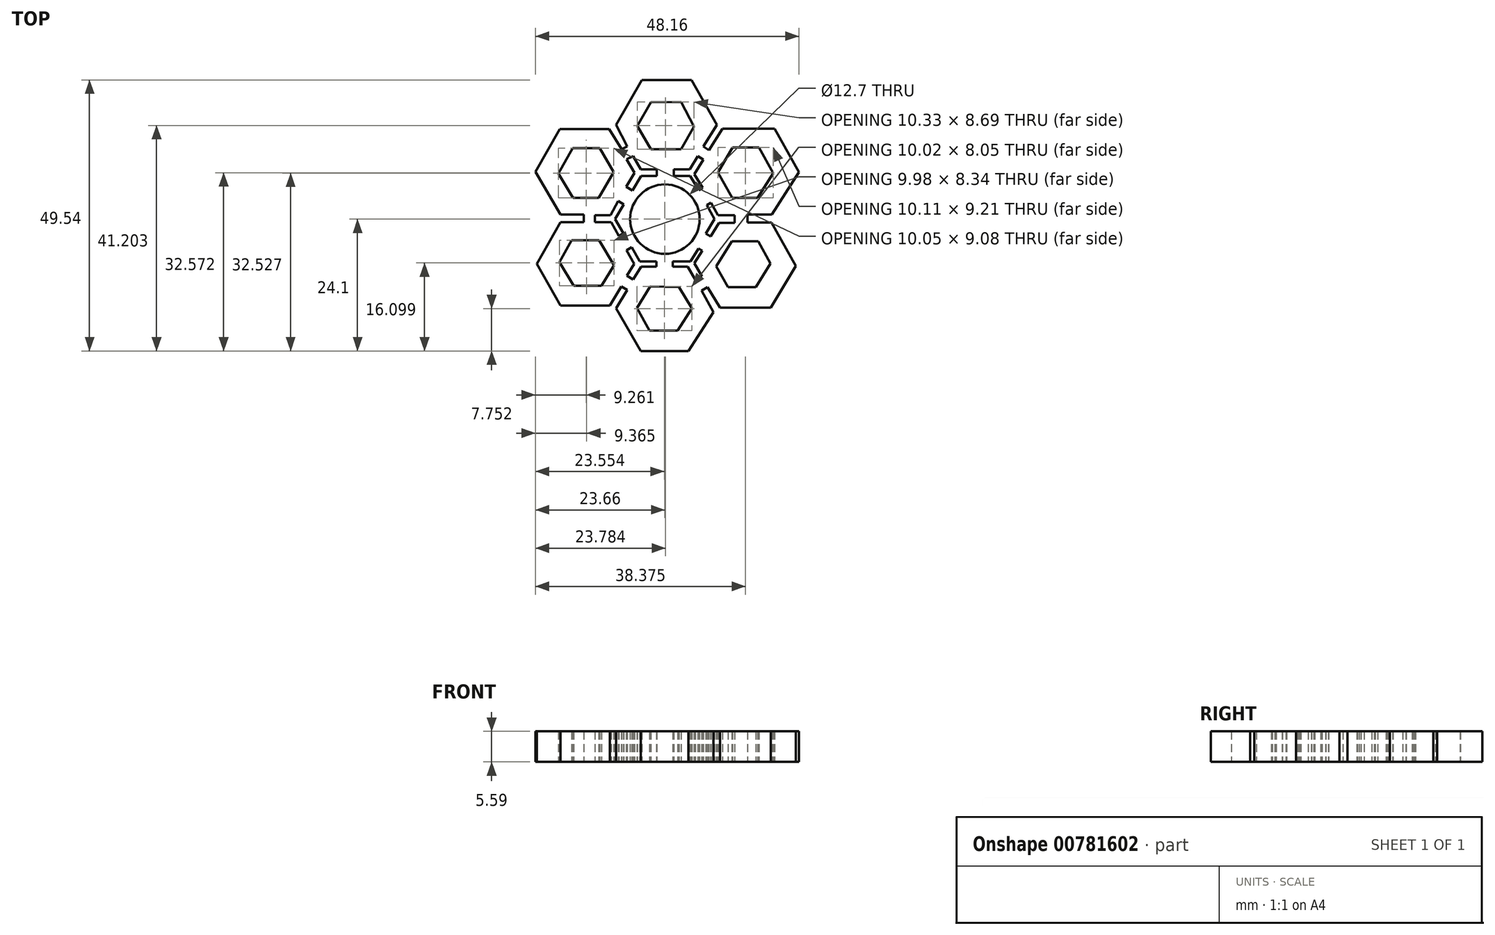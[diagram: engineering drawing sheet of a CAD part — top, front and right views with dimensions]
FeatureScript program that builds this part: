
annotation { "Feature Type Name" : "Feature", "Feature Type Description" : "" }
export const myFeature = defineFeature(function(context is Context, id is Id, definition is map)
    precondition{}
    {
        {
            var Q0;
            Q0=qCreatedBy(makeId("Top.planeOp"),FACE);
            var sketch = newSketch(context, id + "F0", { "sketchPlane" : qUnion([Q0])});
            skCircle(sketch, "E0", {"center": v(0, 0) * mm, "radius": 2.21 * mm});
            skCircle(sketch, "E1", {"center": v(0, 0) * mm, "radius": 6.35 * mm});
            skLineSegment(sketch, "E2", {"start": v(-4.23, 25.44) * mm, "end": v(4.85, 25.44) * mm});
            skLineSegment(sketch, "E3", {"start": v(4.85, 25.44) * mm, "end": v(9.52, 17.24) * mm});
            skLineSegment(sketch, "E4", {"start": v(9.52, 17.24) * mm, "end": v(7.02, 13.29) * mm});
            skLineSegment(sketch, "E5", {"start": v(-4.23, 25.44) * mm, "end": v(-8.93, 17.24) * mm});
            skLineSegment(sketch, "E6", {"start": v(-8.93, 17.24) * mm, "end": v(-6.9, 13.29) * mm});
            skLineSegment(sketch, "E7", {"start": v(7.02, 13.29) * mm, "end": v(8.06, 12.62) * mm});
            skLineSegment(sketch, "E8", {"start": v(8.06, 12.62) * mm, "end": v(10.54, 16.54) * mm});
            skLineSegment(sketch, "E9", {"start": v(-6.9, 13.29) * mm, "end": v(-7.91, 12.76) * mm});
            skPoint(sketch, "E9.endSnap0", {"position": v(-7.91, 15.26) * mm});
            skLineSegment(sketch, "E10", {"start": v(-10.21, 16.49) * mm, "end": v(-7.91, 12.76) * mm});
            skLineSegment(sketch, "E11", {"start": v(-2.54, 21.38) * mm, "end": v(-5.04, 17) * mm});
            skLineSegment(sketch, "E12", {"start": v(-5.04, 17) * mm, "end": v(-2.59, 12.76) * mm});
            skLineSegment(sketch, "E13", {"start": v(-2.59, 12.76) * mm, "end": v(2.96, 12.76) * mm});
            skLineSegment(sketch, "E14", {"start": v(2.96, 12.76) * mm, "end": v(5.3, 16.88) * mm});
            skLineSegment(sketch, "E15", {"start": v(5.3, 16.88) * mm, "end": v(2.93, 21.45) * mm});
            skLineSegment(sketch, "E16", {"start": v(2.93, 21.45) * mm, "end": v(-2.54, 21.38) * mm});
            skLineSegment(sketch, "E17", {"start": v(-6.98, 10.93) * mm, "end": v(-5.8, 11.55) * mm});
            skLineSegment(sketch, "E18", {"start": v(-5.8, 11.55) * mm, "end": v(-4.43, 9.08) * mm});
            skLineSegment(sketch, "E19", {"start": v(-4.43, 9.08) * mm, "end": v(-1.48, 9.11) * mm});
            skLineSegment(sketch, "E20", {"start": v(-1.48, 9.11) * mm, "end": v(-1.46, 7.92) * mm});
            skLineSegment(sketch, "E21", {"start": v(-1.46, 7.92) * mm, "end": v(-4.37, 7.89) * mm});
            skLineSegment(sketch, "E22", {"start": v(-4.37, 7.89) * mm, "end": v(-5.95, 5.25) * mm});
            skLineSegment(sketch, "E23", {"start": v(-5.95, 5.25) * mm, "end": v(-7.05, 5.9) * mm});
            skLineSegment(sketch, "E24", {"start": v(-7.05, 5.9) * mm, "end": v(-5.53, 8.44) * mm});
            skLineSegment(sketch, "E25", {"start": v(-5.53, 8.44) * mm, "end": v(-6.98, 10.93) * mm});
            skLineSegment(sketch, "E26", {"start": v(-10.21, 16.49) * mm, "end": v(-19.24, 16.49) * mm});
            skLineSegment(sketch, "E27", {"start": v(-16.87, 12.97) * mm, "end": v(-11.93, 12.97) * mm});
            skLineSegment(sketch, "E28", {"start": v(-11.93, 12.97) * mm, "end": v(-9.37, 8.57) * mm});
            skLineSegment(sketch, "E29", {"start": v(-9.37, 8.57) * mm, "end": v(-12.06, 3.89) * mm});
            skLineSegment(sketch, "E30", {"start": v(-12.06, 3.89) * mm, "end": v(-16.8, 3.89) * mm});
            skLineSegment(sketch, "E31", {"start": v(-16.8, 3.89) * mm, "end": v(-19.43, 8.34) * mm});
            skLineSegment(sketch, "E32", {"start": v(-19.43, 8.34) * mm, "end": v(-16.87, 12.97) * mm});
            skLineSegment(sketch, "E33", {"start": v(-19.24, 16.49) * mm, "end": v(-23.66, 8.63) * mm});
            skLineSegment(sketch, "E34", {"start": v(-23.66, 8.63) * mm, "end": v(-19.07, 0.84) * mm});
            skLineSegment(sketch, "E35", {"start": v(-19.07, 0.84) * mm, "end": v(-14.8, 0.84) * mm});
            skLineSegment(sketch, "E36", {"start": v(-14.8, 0.84) * mm, "end": v(-14.8, -0.57) * mm});
            skLineSegment(sketch, "E37", {"start": v(-14.8, -0.57) * mm, "end": v(-19.07, -0.57) * mm});
            skLineSegment(sketch, "E38", {"start": v(1.61, 9.11) * mm, "end": v(1.61, 7.92) * mm});
            skLineSegment(sketch, "E39", {"start": v(1.61, 7.92) * mm, "end": v(4.6, 7.92) * mm});
            skLineSegment(sketch, "E40", {"start": v(4.6, 7.92) * mm, "end": v(6.22, 5.3) * mm});
            skLineSegment(sketch, "E41", {"start": v(6.22, 5.3) * mm, "end": v(6.92, 5.72) * mm});
            skLineSegment(sketch, "E42", {"start": v(6.92, 5.72) * mm, "end": v(5.38, 8.22) * mm});
            skLineSegment(sketch, "E43", {"start": v(5.38, 8.22) * mm, "end": v(7, 10.9) * mm});
            skLineSegment(sketch, "E44", {"start": v(7, 10.9) * mm, "end": v(5.98, 11.52) * mm});
            skLineSegment(sketch, "E45", {"start": v(5.98, 11.52) * mm, "end": v(4.53, 9.11) * mm});
            skLineSegment(sketch, "E46", {"start": v(4.53, 9.11) * mm, "end": v(1.61, 9.11) * mm});
            skLineSegment(sketch, "E47", {"start": v(10.54, 16.54) * mm, "end": v(20.05, 16.54) * mm});
            skLineSegment(sketch, "E48", {"start": v(20.05, 16.54) * mm, "end": v(24.5, 8.6) * mm});
            skLineSegment(sketch, "E49", {"start": v(12.37, 13.07) * mm, "end": v(17.15, 13.07) * mm});
            skLineSegment(sketch, "E50", {"start": v(17.15, 13.07) * mm, "end": v(19.77, 8.4) * mm});
            skLineSegment(sketch, "E51", {"start": v(19.77, 8.4) * mm, "end": v(16.9, 3.87) * mm});
            skLineSegment(sketch, "E52", {"start": v(16.9, 3.87) * mm, "end": v(12.27, 3.87) * mm});
            skLineSegment(sketch, "E53", {"start": v(12.27, 3.87) * mm, "end": v(9.66, 8.52) * mm});
            skLineSegment(sketch, "E54", {"start": v(9.66, 8.52) * mm, "end": v(12.37, 13.07) * mm});
            skLineSegment(sketch, "E55", {"start": v(-8.56, 3.3) * mm, "end": v(-7.5, 2.66) * mm});
            skLineSegment(sketch, "E56", {"start": v(-7.5, 2.66) * mm, "end": v(-9.08, 0) * mm});
            skLineSegment(sketch, "E57", {"start": v(-9.08, 0) * mm, "end": v(-7.61, -2.59) * mm});
            skLineSegment(sketch, "E58", {"start": v(-7.61, -2.59) * mm, "end": v(-8.38, -3.12) * mm});
            skLineSegment(sketch, "E59", {"start": v(-8.38, -3.12) * mm, "end": v(-9.8, -0.58) * mm});
            skLineSegment(sketch, "E60", {"start": v(-9.8, -0.58) * mm, "end": v(-12.79, -0.58) * mm});
            skLineSegment(sketch, "E61", {"start": v(-12.79, -0.58) * mm, "end": v(-12.79, 0.74) * mm});
            skLineSegment(sketch, "E62", {"start": v(-12.79, 0.74) * mm, "end": v(-9.93, 0.74) * mm});
            skLineSegment(sketch, "E63", {"start": v(-9.93, 0.74) * mm, "end": v(-8.56, 3.3) * mm});
            skLineSegment(sketch, "E64", {"start": v(7.68, 2.55) * mm, "end": v(8.43, 2.98) * mm});
            skPoint(sketch, "E64.endSnap0", {"position": v(-8.03, 2.98) * mm});
            skLineSegment(sketch, "E65", {"start": v(8.43, 2.98) * mm, "end": v(9.7, 0.73) * mm});
            skLineSegment(sketch, "E66", {"start": v(9.7, 0.73) * mm, "end": v(12.74, 0.73) * mm});
            skLineSegment(sketch, "E67", {"start": v(12.74, 0.73) * mm, "end": v(12.74, -0.67) * mm});
            skLineSegment(sketch, "E68", {"start": v(12.74, -0.67) * mm, "end": v(9.85, -0.67) * mm});
            skLineSegment(sketch, "E69", {"start": v(9.85, -0.67) * mm, "end": v(8.36, -3.17) * mm});
            skLineSegment(sketch, "E70", {"start": v(8.36, -3.17) * mm, "end": v(7.48, -2.64) * mm});
            skLineSegment(sketch, "E71", {"start": v(7.48, -2.64) * mm, "end": v(9.05, 0) * mm});
            skLineSegment(sketch, "E72", {"start": v(9.05, 0) * mm, "end": v(7.68, 2.55) * mm});
            skLineSegment(sketch, "E73", {"start": v(24.5, 8.6) * mm, "end": v(19.56, 0.82) * mm});
            skLineSegment(sketch, "E74", {"start": v(19.56, 0.82) * mm, "end": v(15.06, 0.82) * mm});
            skLineSegment(sketch, "E75", {"start": v(15.06, 0.82) * mm, "end": v(15.06, -0.61) * mm});
            skLineSegment(sketch, "E76", {"start": v(15.06, -0.61) * mm, "end": v(19.45, -0.61) * mm});
            skLineSegment(sketch, "E77", {"start": v(19.45, -0.61) * mm, "end": v(23.9, -8.54) * mm});
            skLineSegment(sketch, "E78", {"start": v(-19.07, -0.57) * mm, "end": v(-23.37, -8.17) * mm});
            skLineSegment(sketch, "E79", {"start": v(-17.05, -3.83) * mm, "end": v(-12.06, -3.83) * mm});
            skLineSegment(sketch, "E80", {"start": v(-12.06, -3.83) * mm, "end": v(-9.3, -8.43) * mm});
            skLineSegment(sketch, "E81", {"start": v(-9.3, -8.43) * mm, "end": v(-11.58, -12.17) * mm});
            skLineSegment(sketch, "E82", {"start": v(-11.58, -12.17) * mm, "end": v(-16.66, -12.17) * mm});
            skLineSegment(sketch, "E83", {"start": v(-16.66, -12.17) * mm, "end": v(-19.28, -7.83) * mm});
            skLineSegment(sketch, "E84", {"start": v(-19.28, -7.83) * mm, "end": v(-17.05, -3.83) * mm});
            skLineSegment(sketch, "E85", {"start": v(-8, -12.28) * mm, "end": v(-10.06, -15.8) * mm});
            skLineSegment(sketch, "E86", {"start": v(-10.06, -15.8) * mm, "end": v(-19.05, -15.8) * mm});
            skLineSegment(sketch, "E87", {"start": v(-19.05, -15.8) * mm, "end": v(-23.37, -8.17) * mm});
            skLineSegment(sketch, "E88", {"start": v(-6.99, -5.7) * mm, "end": v(-6.05, -5.15) * mm});
            skLineSegment(sketch, "E89", {"start": v(-6.05, -5.15) * mm, "end": v(-4.57, -7.7) * mm});
            skLineSegment(sketch, "E90", {"start": v(-4.57, -7.7) * mm, "end": v(-1.56, -7.7) * mm});
            skLineSegment(sketch, "E91", {"start": v(-1.56, -7.7) * mm, "end": v(-1.56, -8.66) * mm});
            skLineSegment(sketch, "E92", {"start": v(-1.56, -8.66) * mm, "end": v(-4.35, -8.66) * mm});
            skLineSegment(sketch, "E93", {"start": v(-4.35, -8.66) * mm, "end": v(-5.78, -11.02) * mm});
            skLineSegment(sketch, "E94", {"start": v(-5.78, -11.02) * mm, "end": v(-6.93, -10.32) * mm});
            skLineSegment(sketch, "E95", {"start": v(-6.93, -10.32) * mm, "end": v(-5.61, -8.15) * mm});
            skLineSegment(sketch, "E96", {"start": v(-5.61, -8.15) * mm, "end": v(-6.99, -5.7) * mm});
            skLineSegment(sketch, "E97", {"start": v(-8, -12.28) * mm, "end": v(-6.92, -12.9) * mm});
            skLineSegment(sketch, "E98", {"start": v(-6.92, -12.9) * mm, "end": v(-8.92, -16.32) * mm});
            skLineSegment(sketch, "E99", {"start": v(1.43, -7.7) * mm, "end": v(1.43, -8.66) * mm});
            skLineSegment(sketch, "E100", {"start": v(1.43, -8.66) * mm, "end": v(4.18, -8.66) * mm});
            skLineSegment(sketch, "E101", {"start": v(4.18, -8.66) * mm, "end": v(5.56, -11.1) * mm});
            skLineSegment(sketch, "E102", {"start": v(5.56, -11.1) * mm, "end": v(6.74, -10.43) * mm});
            skLineSegment(sketch, "E103", {"start": v(6.74, -10.43) * mm, "end": v(5.4, -8.04) * mm});
            skLineSegment(sketch, "E104", {"start": v(5.4, -8.04) * mm, "end": v(6.81, -5.78) * mm});
            skLineSegment(sketch, "E105", {"start": v(6.81, -5.78) * mm, "end": v(6.12, -5.35) * mm});
            skLineSegment(sketch, "E106", {"start": v(6.12, -5.35) * mm, "end": v(4.65, -7.7) * mm});
            skLineSegment(sketch, "E107", {"start": v(4.65, -7.7) * mm, "end": v(1.43, -7.7) * mm});
            skLineSegment(sketch, "E108", {"start": v(2.56, -12.42) * mm, "end": v(4.9, -16.28) * mm});
            skLineSegment(sketch, "E109", {"start": v(4.9, -16.28) * mm, "end": v(2.35, -20.37) * mm});
            skLineSegment(sketch, "E110", {"start": v(2.35, -20.37) * mm, "end": v(-2.8, -20.37) * mm});
            skLineSegment(sketch, "E111", {"start": v(-2.8, -20.37) * mm, "end": v(-5.11, -16.23) * mm});
            skLineSegment(sketch, "E112", {"start": v(-5.11, -16.23) * mm, "end": v(-2.67, -12.32) * mm});
            skLineSegment(sketch, "E113", {"start": v(-2.67, -12.32) * mm, "end": v(2.56, -12.42) * mm});
            skLineSegment(sketch, "E114", {"start": v(6.7, -13.08) * mm, "end": v(7.8, -12.42) * mm});
            skLineSegment(sketch, "E115", {"start": v(-8.92, -16.32) * mm, "end": v(-4.43, -24.1) * mm});
            skLineSegment(sketch, "E116", {"start": v(-4.43, -24.1) * mm, "end": v(4.3, -24.1) * mm});
            skLineSegment(sketch, "E117", {"start": v(4.3, -24.1) * mm, "end": v(8.84, -16.97) * mm});
            skLineSegment(sketch, "E118", {"start": v(8.84, -16.97) * mm, "end": v(6.7, -13.08) * mm});
            skLineSegment(sketch, "E119", {"start": v(9.38, -8.63) * mm, "end": v(11.51, -12.44) * mm});
            skLineSegment(sketch, "E120", {"start": v(11.51, -12.44) * mm, "end": v(16.6, -12.44) * mm});
            skLineSegment(sketch, "E121", {"start": v(16.6, -12.44) * mm, "end": v(19.27, -8.13) * mm});
            skLineSegment(sketch, "E122", {"start": v(19.27, -8.13) * mm, "end": v(17.04, -4.05) * mm});
            skLineSegment(sketch, "E123", {"start": v(17.04, -4.05) * mm, "end": v(12.2, -4.05) * mm});
            skLineSegment(sketch, "E124", {"start": v(12.2, -4.05) * mm, "end": v(9.38, -8.63) * mm});
            skLineSegment(sketch, "E125", {"start": v(7.8, -12.42) * mm, "end": v(10.08, -16.2) * mm});
            skLineSegment(sketch, "E126", {"start": v(10.08, -16.2) * mm, "end": v(19.34, -16.2) * mm});
            skLineSegment(sketch, "E127", {"start": v(19.34, -16.2) * mm, "end": v(23.9, -8.54) * mm});
            skSolve(sketch);
        }
        {
            var Q0;
            Q0=makeQuery(id+"F0.imprint","IMPRINT",FACE,{"disambiguationData":[TD([[makeQuery(id+"F0.imprint","IMPRINT",EDGE,{"derivedFrom":sQuery(id+"F0.wireOp",EDGE,"E1")}),-1.0]])]});
            extrude(context, id + "F1", {"entities" : qUnion([Q0]), "depth" : 5.6 * mm, "offsetDistance" : 25.4 * mm});
        }
    });
